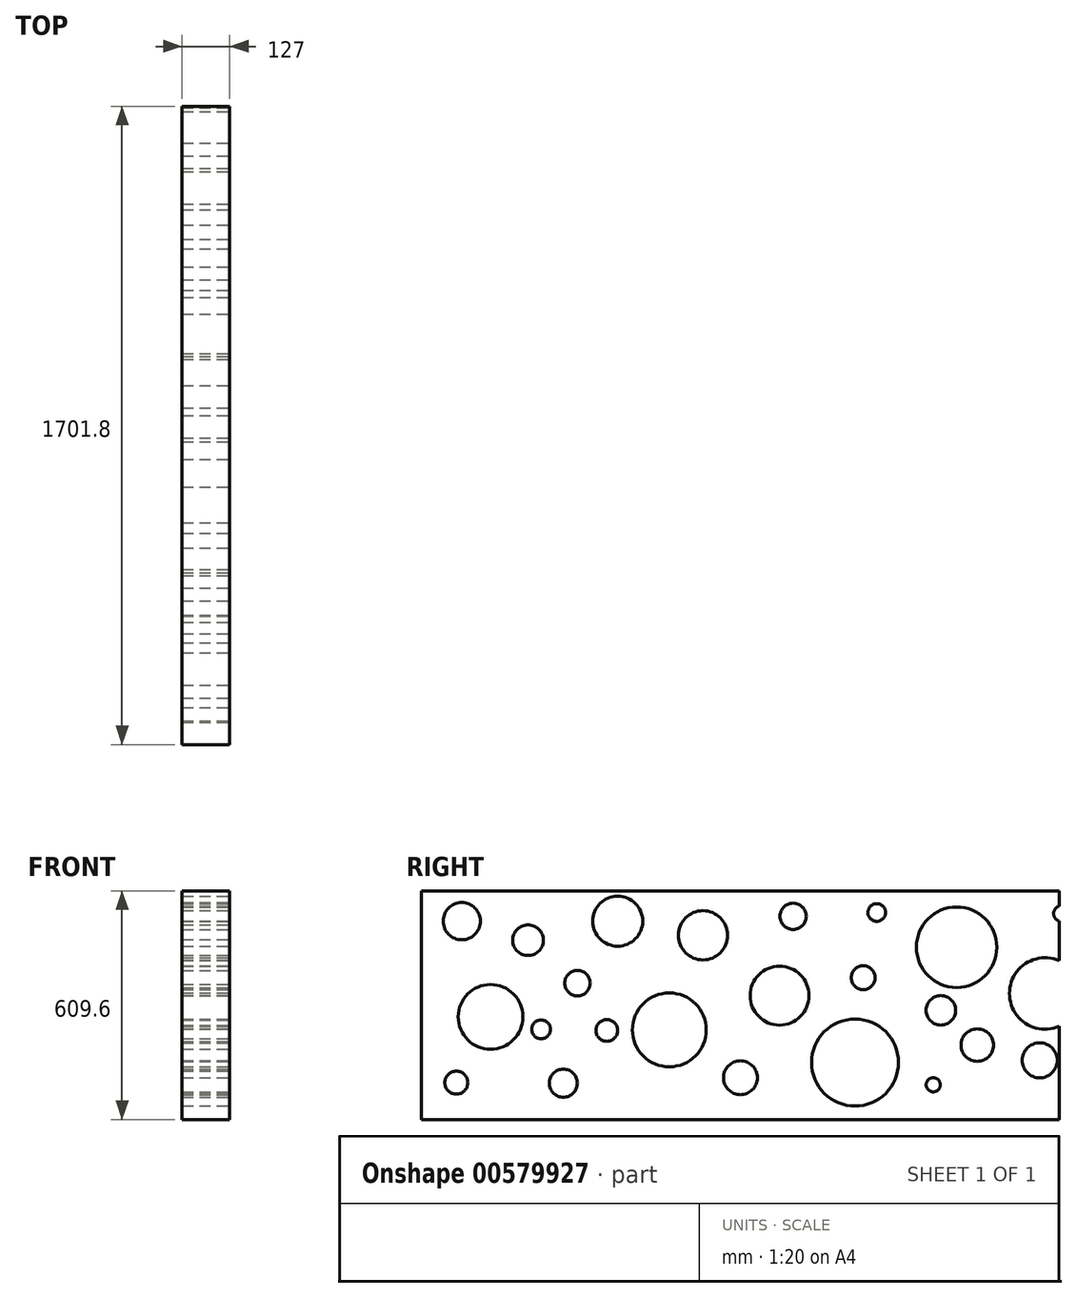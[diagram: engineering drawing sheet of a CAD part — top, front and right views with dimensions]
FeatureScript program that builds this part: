
annotation { "Feature Type Name" : "Feature", "Feature Type Description" : "" }
export const myFeature = defineFeature(function(context is Context, id is Id, definition is map)
    precondition{}
    {
        {
            var Q0;
            Q0=qCreatedBy(makeId("Top.planeOp"),FACE);
            var sketch = newSketch(context, id + "F0", { "sketchPlane" : qUnion([Q0])});
            skLineSegment(sketch, "E0.bottom", {"start": v(-107.93, 796.77) * mm, "end": v(19.07, 796.77) * mm});
            skLineSegment(sketch, "E0.top", {"start": v(-107.93, -905.03) * mm, "end": v(19.07, -905.03) * mm});
            skLineSegment(sketch, "E0.left", {"start": v(-107.93, 796.77) * mm, "end": v(-107.93, -905.03) * mm});
            skLineSegment(sketch, "E0.right", {"start": v(19.07, 796.77) * mm, "end": v(19.07, -905.03) * mm});
            skSolve(sketch);
        }
        {
            var Q0;
            Q0=makeQuery(id+"F0.imprint","IMPRINT",FACE,{"disambiguationData":[TD([[makeQuery(id+"F0.imprint","IMPRINT",EDGE,{"derivedFrom":sQuery(id+"F0.wireOp",EDGE,"E0.bottom")}),-1.0]])]});
            extrude(context, id + "F1", {"entities" : qUnion([Q0]), "depth" : 609.6 * mm, "offsetDistance" : 25.4 * mm});
        }
        {
            var Q0;
            Q0=makeQuery(id+"F1.opExtrude","SWEPT_FACE",FACE,{"disambiguationData":[OSD([sQuery(id+"F0.wireOp",EDGE,"E0.right")])]});
            var sketch = newSketch(context, id + "F2", { "sketchPlane" : qUnion([Q0])});
            skCircle(sketch, "E1", {"center": v(-796.77, 528.65) * mm, "radius": 49.57 * mm});
            skCircle(sketch, "E2", {"center": v(-719.96, 273.58) * mm, "radius": 86.29 * mm});
            skCircle(sketch, "E3", {"center": v(-525.76, 96.78) * mm, "radius": 37.4 * mm});
            skCircle(sketch, "E4", {"center": v(-488.08, 363.44) * mm, "radius": 33.93 * mm});
            skCircle(sketch, "E5", {"center": v(-619.96, 477.93) * mm, "radius": 40.84 * mm});
            skCircle(sketch, "E6", {"center": v(-811.26, 98.23) * mm, "radius": 30.7 * mm});
            skCircle(sketch, "E7", {"center": v(-243.16, 238.8) * mm, "radius": 98.46 * mm});
            skCircle(sketch, "E8", {"center": v(-380.84, 528.65) * mm, "radius": 66.68 * mm});
            skCircle(sketch, "E9", {"center": v(51.03, 330.1) * mm, "radius": 78.55 * mm});
            skCircle(sketch, "E10", {"center": v(-153.3, 490.97) * mm, "radius": 65.71 * mm});
            skCircle(sketch, "E11", {"center": v(-53.31, 111.27) * mm, "radius": 45.14 * mm});
            skCircle(sketch, "E12", {"center": v(252.48, 151.85) * mm, "radius": 116.03 * mm});
            skCircle(sketch, "E13", {"center": v(274.22, 377.93) * mm, "radius": 31.82 * mm});
            skCircle(sketch, "E14", {"center": v(87.26, 541.7) * mm, "radius": 35.08 * mm});
            skCircle(sketch, "E15", {"center": v(523.49, 459.09) * mm, "radius": 107.33 * mm});
            skCircle(sketch, "E16", {"center": v(310.45, 551.84) * mm, "radius": 23.6 * mm});
            skCircle(sketch, "E17", {"center": v(481.46, 290.97) * mm, "radius": 39.42 * mm});
            skCircle(sketch, "E18", {"center": v(578.56, 198.22) * mm, "radius": 43.23 * mm});
            skCircle(sketch, "E19", {"center": v(461.17, 92.43) * mm, "radius": 18.9 * mm});
            skCircle(sketch, "E20", {"center": v(759.71, 335.9) * mm, "radius": 95.3 * mm});
            skCircle(sketch, "E21", {"center": v(803.19, 548.94) * mm, "radius": 20.9 * mm});
            skCircle(sketch, "E22", {"center": v(745.22, 157.64) * mm, "radius": 46.74 * mm});
            skCircle(sketch, "E23", {"center": v(-585.18, 240.25) * mm, "radius": 24.93 * mm});
            skCircle(sketch, "E24", {"center": v(-409.82, 237.35) * mm, "radius": 29.02 * mm});
            skSolve(sketch);
        }
        {
            var Q0;
            Q0 = qSketchRegion(id + "F2", true);
            extrude(context, id + "F3", {"entities" : qUnion([Q0]), "operationType" : NewBodyOperationType.REMOVE, "oppositeDirection" : true, "depth" : 127 * mm, "offsetDistance" : 25.4 * mm});
        }
    });
